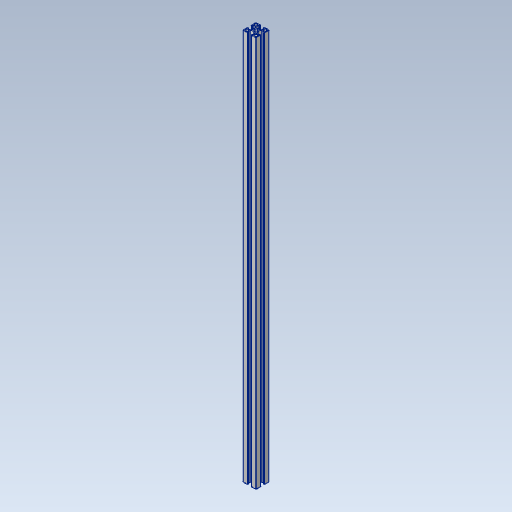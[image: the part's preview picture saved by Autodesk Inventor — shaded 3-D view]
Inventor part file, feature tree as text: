
AUTODESK INVENTOR PART (.ipt)
format: ipt  version: 2021 (Build 250183000, 183)  size: 212,480 bytes
history: native  units: mm
features: other x3, extrude x1
ambient origin geometry x8: Origin, YZ Plane, XZ Plane, XY Plane, X Axis, Y Axis, Z Axis, Center Point
bodies: Body1 (feature_tree)
feature tree (4):
  other  "솔리드1"
  other  "df_2020.dwg"
  extrude  "600mm 2020"  Depth=600.0mm TaperAngle=0.0deg
  other  "2020_Base"
